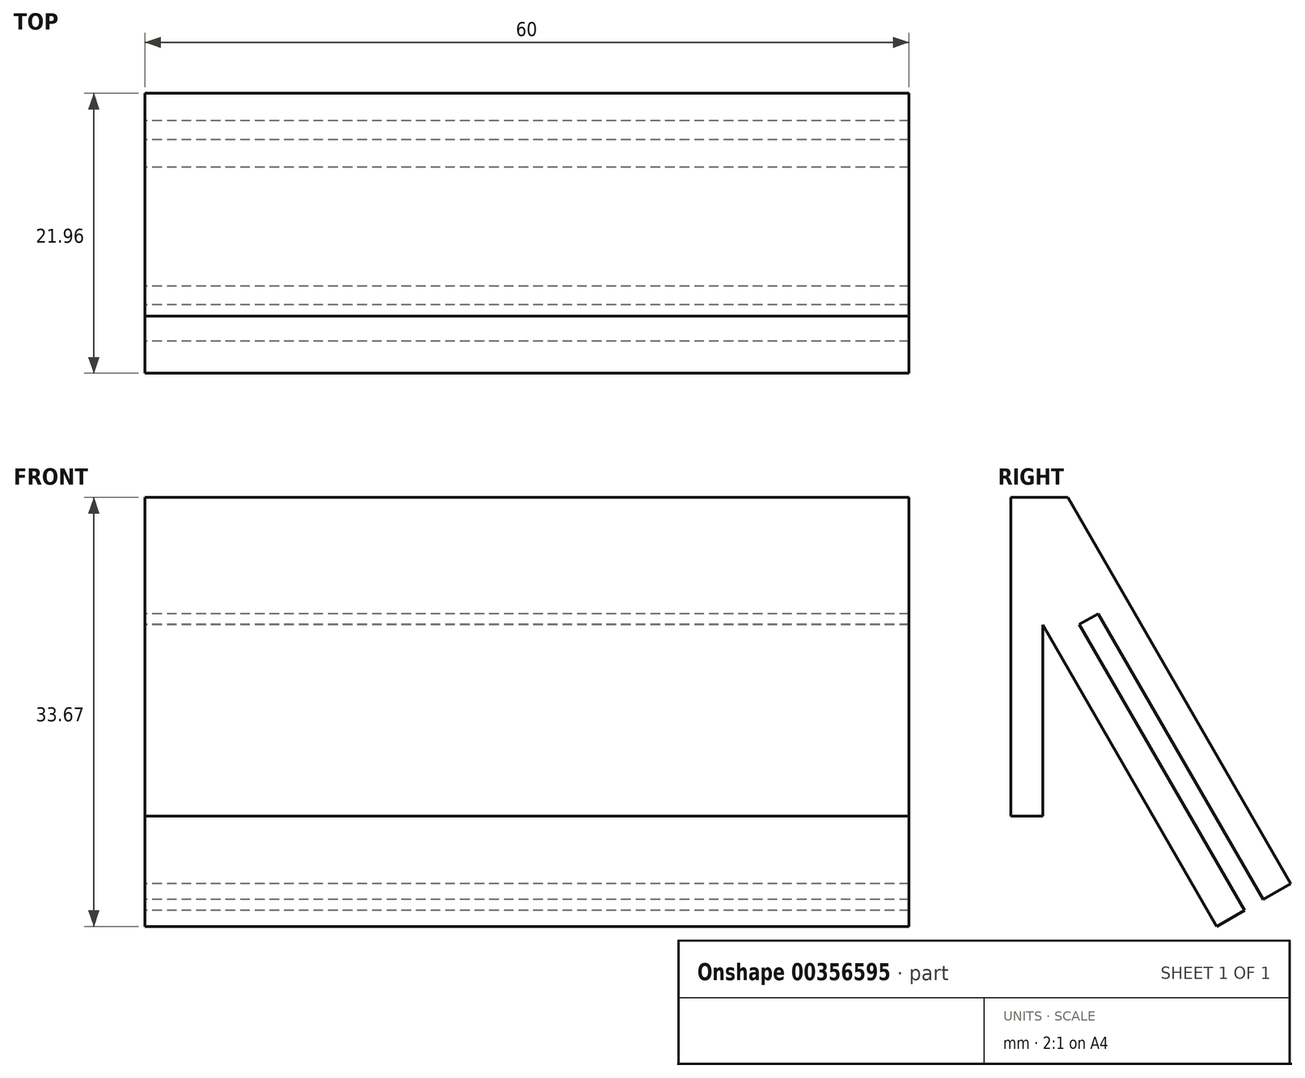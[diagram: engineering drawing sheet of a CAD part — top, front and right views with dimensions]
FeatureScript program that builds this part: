
annotation { "Feature Type Name" : "Feature", "Feature Type Description" : "" }
export const myFeature = defineFeature(function(context is Context, id is Id, definition is map)
    precondition{}
    {
        {
            var Q0;
            Q0=qCreatedBy(makeId("Right.planeOp"),FACE);
            var sketch = newSketch(context, id + "F0", { "sketchPlane" : qUnion([Q0])});
            skLineSegment(sketch, "E0", {"start": v(0, 0) * mm, "end": v(4.46, 0) * mm});
            skLineSegment(sketch, "E1", {"start": v(4.46, 0) * mm, "end": v(21.96, -30.31) * mm});
            skLineSegment(sketch, "E2", {"start": v(0, 0) * mm, "end": v(0, -25) * mm});
            skLineSegment(sketch, "E3", {"start": v(0, -25) * mm, "end": v(2.5, -25) * mm});
            skLineSegment(sketch, "E4", {"start": v(2.5, -25) * mm, "end": v(2.5, -10) * mm});
            skLineSegment(sketch, "E5", {"start": v(21.96, -30.31) * mm, "end": v(19.8, -31.56) * mm});
            skLineSegment(sketch, "E6", {"start": v(19.8, -31.56) * mm, "end": v(6.84, -9.12) * mm});
            skLineSegment(sketch, "E7", {"start": v(6.84, -9.12) * mm, "end": v(5.37, -9.97) * mm});
            skLineSegment(sketch, "E8", {"start": v(5.37, -9.97) * mm, "end": v(18.33, -32.42) * mm});
            skLineSegment(sketch, "E9", {"start": v(18.33, -32.42) * mm, "end": v(16.16, -33.67) * mm});
            skLineSegment(sketch, "E10", {"start": v(16.16, -33.67) * mm, "end": v(2.5, -10) * mm});
            skSolve(sketch);
        }
        {
            var Q0;
            Q0 = qSketchRegion(id + "F0", true);
            extrude(context, id + "F1", {"entities" : qUnion([Q0]), "depth" : 60 * mm});
        }
    });
